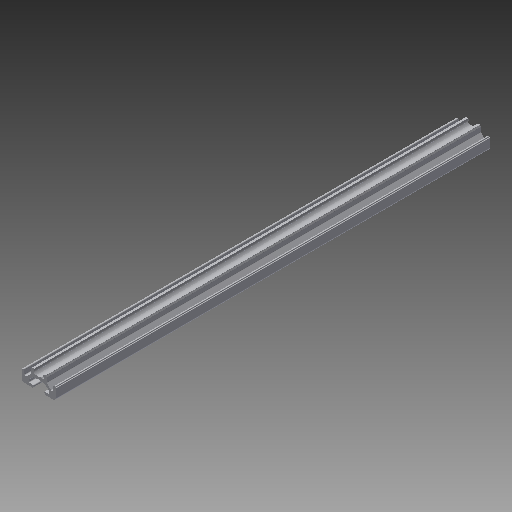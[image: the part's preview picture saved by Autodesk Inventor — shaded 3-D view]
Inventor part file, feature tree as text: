
AUTODESK INVENTOR PART (.ipt)
format: ipt  version: 2019 (Build 230136000, 136)  size: 342,528 bytes
history: native  units: in
note: dims shown in document units (in); Inventor stores cm internally (conversion verified against a paired STEP export)
features: other x3, extrude x2, sketch x2, thicken_offset x1
ambient origin geometry x8: Origin, YZ Plane, XZ Plane, XY Plane, X Axis, Y Axis, Z Axis, Center Point
bodies: Solid1 (feature_tree)
feature tree (8):
  other  "Blocks"
  extrude  "Extrusion1"  Depth=4.5in
  thicken_offset  "Thicken1"
  extrude  "Extrusion3"  Depth=0.3935in TaperAngle=0.0deg
  sketch  "Sketch1"  dims[d1=0.0in d5=4.5in]
  other  "20x20"
  sketch  "Sketch3"  dims[d6=4.5in d7=0.3935in d8=0.0in]
  other  "20x20:1"
